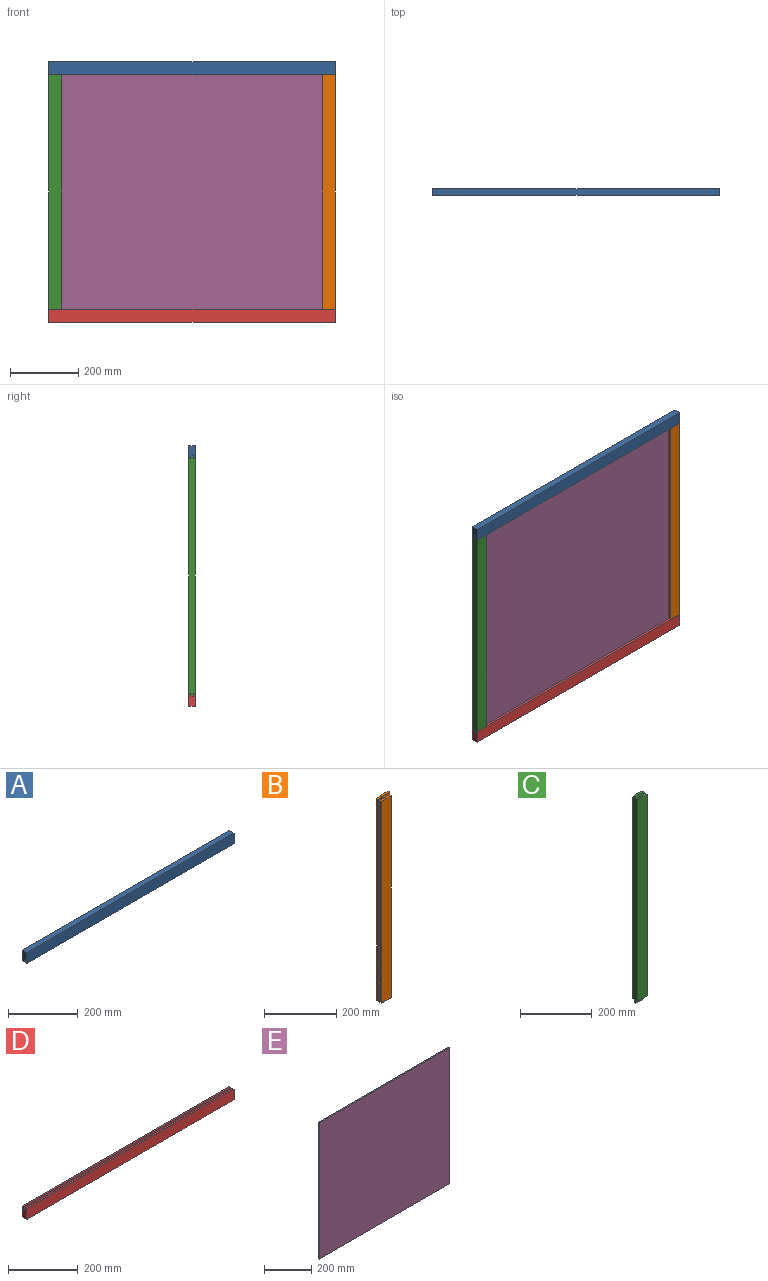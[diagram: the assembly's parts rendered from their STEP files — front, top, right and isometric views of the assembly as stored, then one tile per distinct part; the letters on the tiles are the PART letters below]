
ASSEMBLY  parts=5 mates=4
PART A: 10 faces, bbox 838.2x19.1x38.1 mm
  f0: plane 838.2x38.1mm, normal (0,-1,0), area 31935.4mm2, adj f1,f7,f8,f9
  f1: plane 838.2x6.35mm, normal (0,0,-1), area 5322.6mm2, adj f0,f2,f8,f9
  f2: plane 838.2x9.53mm, normal (0,1,0), area 7983.9mm2, adj f1,f3,f8,f9
  f3: plane 838.2x6.35mm, normal (0,0,-1), area 5322.6mm2, adj f2,f4,f8,f9
  f4: plane 838.2x9.53mm, normal (0,-1,0), area 7983.9mm2, adj f3,f5,f8,f9
  f5: plane 838.2x6.35mm, normal (0,0,-1), area 5322.6mm2, adj f4,f6,f8,f9
  f6: plane 838.2x38.1mm, normal (0,1,0), area 31935.4mm2, adj f5,f7,f8,f9
  f7: plane 838.2x19.05mm, normal (0,0,1), area 15967.7mm2, adj f0,f6,f8,f9
  f8: plane 38.1x19.05mm, normal (1,0,0), area 665.3mm2, adj f0,f1,f2,f3,f4,f5,f6,f7
  f9: plane 38.1x19.05mm, normal (-1,0,0), area 665.3mm2, adj f0,f1,f2,f3,f4,f5,f6,f7
PART B: 18 faces, bbox 38.1x19.1x702.3 mm
  f0: plane 38.1x6.35mm, normal (0,0,-1), area 241.9mm2, adj f2,f3,f4,f5,f15
  f1: plane 38.1x6.35mm, normal (0,0,1), area 241.9mm2, adj f2,f3,f4,f5,f13
  f2: plane 702.31x19.05mm, normal (1,0,0), area 13169.3mm2, adj f0,f1,f3,f9,f10,f11,f12,f13
  f3: plane 685.8x38.1mm, normal (0,1,0), area 26129mm2, adj f0,f1,f2,f4
  f4: plane 685.8x6.35mm, normal (-1,0,0), area 4354.8mm2, adj f0,f1,f3,f5
  f5: plane 685.8x9.53mm, normal (0,-1,0), area 6532.2mm2, adj f0,f1,f4,f6
  f6: plane 702.31x6.35mm, normal (-1,0,0), area 4459.7mm2, adj f5,f7,f12,f13,f14,f15,f16,f17
  f7: plane 685.8x9.53mm, normal (0,1,0), area 6532.2mm2, adj f6,f8,f10,f11
  f8: plane 685.8x6.35mm, normal (-1,0,0), area 4354.8mm2, adj f7,f9,f10,f11
  f9: plane 685.8x38.1mm, normal (0,-1,0), area 26129mm2, adj f2,f8,f10,f11
  f10: plane 38.1x6.35mm, normal (0,0,1), area 241.9mm2, adj f2,f7,f8,f9,f12
  f11: plane 38.1x6.35mm, normal (0,0,-1), area 241.9mm2, adj f2,f7,f8,f9,f16
  f12: plane 28.58x9.53mm, normal (0,-1,0), area 272.2mm2, adj f2,f6,f10,f14
  f13: plane 28.58x9.53mm, normal (0,1,0), area 272.2mm2, adj f1,f2,f6,f14
  f14: plane 28.58x6.35mm, normal (0,0,1), area 181.5mm2, adj f2,f6,f12,f13
  f15: plane 28.58x6.99mm, normal (0,1,0), area 199.6mm2, adj f0,f2,f6,f17
  f16: plane 28.58x6.99mm, normal (0,-1,0), area 199.6mm2, adj f2,f6,f11,f17
  f17: plane 28.58x6.35mm, normal (0,0,-1), area 181.5mm2, adj f2,f6,f15,f16
PART C: 18 faces, bbox 38.1x19.1x704.9 mm
  f0: plane 38.1x6.35mm, normal (0,0,-1), area 241.9mm2, adj f2,f3,f4,f5,f15
  f1: plane 38.1x6.35mm, normal (0,0,1), area 241.9mm2, adj f2,f3,f4,f5,f13
  f2: plane 704.85x19.05mm, normal (-1,0,0), area 13185.5mm2, adj f0,f1,f3,f9,f10,f11,f12,f13
  f3: plane 685.8x38.1mm, normal (0,-1,0), area 26129mm2, adj f0,f1,f2,f4
  f4: plane 685.8x6.35mm, normal (1,0,0), area 4354.8mm2, adj f0,f1,f3,f5
  f5: plane 685.8x9.53mm, normal (0,1,0), area 6532.2mm2, adj f0,f1,f4,f6
  f6: plane 704.85x6.35mm, normal (1,0,0), area 4475.8mm2, adj f5,f7,f12,f13,f14,f15,f16,f17
  f7: plane 685.8x9.53mm, normal (0,-1,0), area 6532.2mm2, adj f6,f8,f10,f11
  f8: plane 685.8x6.35mm, normal (1,0,0), area 4354.8mm2, adj f7,f9,f10,f11
  f9: plane 685.8x38.1mm, normal (0,1,0), area 26129mm2, adj f2,f8,f10,f11
  f10: plane 38.1x6.35mm, normal (0,0,1), area 241.9mm2, adj f2,f7,f8,f9,f12
  f11: plane 38.1x6.35mm, normal (0,0,-1), area 241.9mm2, adj f2,f7,f8,f9,f16
  f12: plane 28.58x9.53mm, normal (0,1,0), area 272.2mm2, adj f2,f6,f10,f14
  f13: plane 28.58x9.53mm, normal (0,-1,0), area 272.2mm2, adj f1,f2,f6,f14
  f14: plane 28.58x6.35mm, normal (0,0,1), area 181.5mm2, adj f2,f6,f12,f13
  f15: plane 28.58x9.53mm, normal (0,-1,0), area 272.2mm2, adj f0,f2,f6,f17
  f16: plane 28.58x9.53mm, normal (0,1,0), area 272.2mm2, adj f2,f6,f11,f17
  f17: plane 28.58x6.35mm, normal (0,0,-1), area 181.5mm2, adj f2,f6,f15,f16
PART D: 10 faces, bbox 838.2x19.1x38.1 mm
  f0: plane 838.2x38.1mm, normal (0,1,0), area 31935.4mm2, adj f1,f7,f8,f9
  f1: plane 838.2x6.35mm, normal (0,0,1), area 5322.6mm2, adj f0,f2,f8,f9
  f2: plane 838.2x9.53mm, normal (0,-1,0), area 7983.9mm2, adj f1,f3,f8,f9
  f3: plane 838.2x6.35mm, normal (0,0,1), area 5322.6mm2, adj f2,f4,f8,f9
  f4: plane 838.2x9.53mm, normal (0,1,0), area 7983.9mm2, adj f3,f5,f8,f9
  f5: plane 838.2x6.35mm, normal (0,0,1), area 5322.6mm2, adj f4,f6,f8,f9
  f6: plane 838.2x38.1mm, normal (0,-1,0), area 31935.4mm2, adj f5,f7,f8,f9
  f7: plane 838.2x19.05mm, normal (0,0,-1), area 15967.7mm2, adj f0,f6,f8,f9
  f8: plane 38.1x19.05mm, normal (1,0,0), area 665.3mm2, adj f0,f1,f2,f3,f4,f5,f6,f7
  f9: plane 38.1x19.05mm, normal (-1,0,0), area 665.3mm2, adj f0,f1,f2,f3,f4,f5,f6,f7
PART E: 6 faces, bbox 781.1x6.4x704.9 mm
  f0: plane 704.85x6.35mm, normal (-1,0,0), area 4475.8mm2, adj f1,f3,f4,f5
  f1: plane 781.05x6.35mm, normal (0,0,-1), area 4959.7mm2, adj f0,f2,f4,f5
  f2: plane 704.85x6.35mm, normal (1,0,0), area 4475.8mm2, adj f1,f3,f4,f5
  f3: plane 781.05x6.35mm, normal (0,0,1), area 4959.7mm2, adj f0,f2,f4,f5
  f4: plane 781.05x704.85mm, normal (0,-1,0), area 550523.1mm2, adj f0,f1,f2,f3
  f5: plane 781.05x704.85mm, normal (0,1,0), area 550523.1mm2, adj f0,f1,f2,f3
PLACE A t=(0,0,685.8)mm
PLACE B t=(838.2,19.05,0)mm
PLACE C at identity
PLACE D t=(0,19.05,-76.2)mm
PLACE E t=(88.16,12.7,45.51)mm
MATE fastened D.f6 <-> C.f3  axis (0,-1,0) through (0,0,0)mm
MATE fastened B.f9 <-> C.f3  axis (0,-1,0) through (800.1,0,685.8)mm
MATE fastened A.f0 <-> C.f3  axis (0,-1,0) through (0,0,685.8)mm
MATE fastened E.f3 <-> C.f14  axis (0,0,1) through (28.58,12.7,695.32)mm
